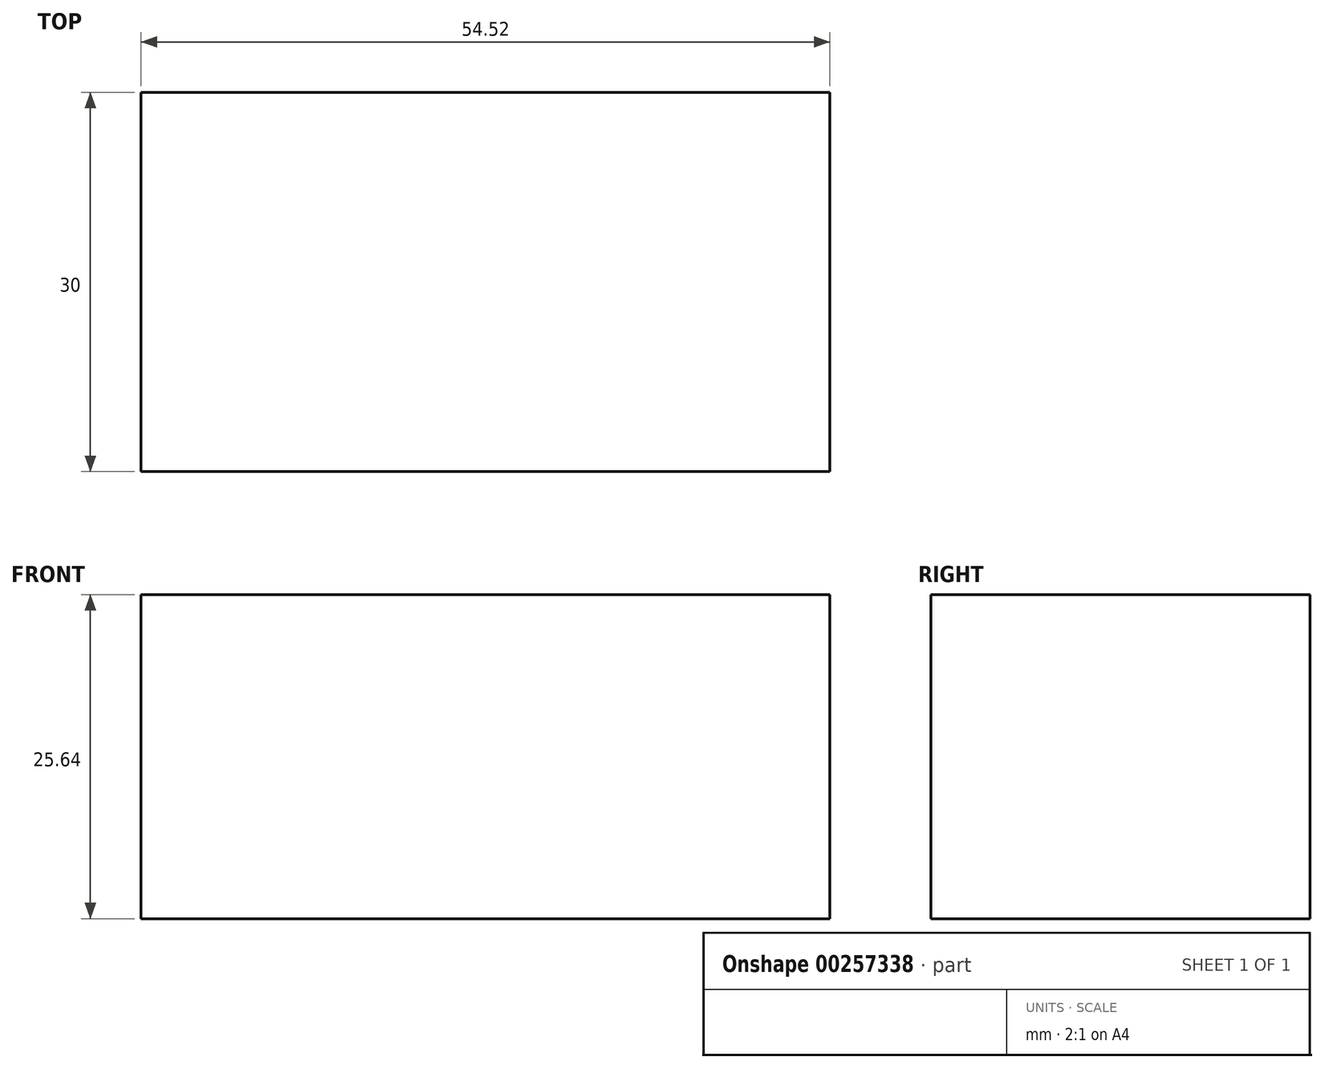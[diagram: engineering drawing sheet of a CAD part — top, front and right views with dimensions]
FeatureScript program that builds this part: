
annotation { "Feature Type Name" : "Feature", "Feature Type Description" : "" }
export const myFeature = defineFeature(function(context is Context, id is Id, definition is map)
    precondition{}
    {
        {
            var Q0;
            Q0=qCreatedBy(makeId("Front.planeOp"),FACE);
            var sketch = newSketch(context, id + "F0", { "sketchPlane" : qUnion([Q0])});
            skLineSegment(sketch, "E0.bottom", {"start": v(0, 0) * mm, "end": v(27.26, 0) * mm});
            skLineSegment(sketch, "E0.top", {"start": v(0, 25.64) * mm, "end": v(27.26, 25.64) * mm});
            skLineSegment(sketch, "E0.left", {"start": v(0, 0) * mm, "end": v(0, 25.64) * mm});
            skLineSegment(sketch, "E0.right", {"start": v(27.26, 0) * mm, "end": v(27.26, 25.64) * mm});
            skSolve(sketch);
        }
        {
            var Q0;
            Q0=makeQuery(id+"F0.imprint","IMPRINT",FACE,{"disambiguationData":[TD([[makeQuery(id+"F0.imprint","IMPRINT",EDGE,{"derivedFrom":sQuery(id+"F0.wireOp",EDGE,"E0.bottom")}),1.0]])]});
            extrude(context, id + "F1", {"entities" : qUnion([Q0]), "depth" : 30 * mm});
        }
        {
            var Q0;
            Q0=makeQuery(id+"F1.opExtrude","SWEPT_BODY",BODY,{"disambiguationData":[OSD([sQuery(id+"F0.wireOp",EDGE,"E0.bottom"),sQuery(id+"F0.wireOp",EDGE,"E0.top"),sQuery(id+"F0.wireOp",EDGE,"E0.left"),sQuery(id+"F0.wireOp",EDGE,"E0.right")])]});
            var Q1;
            Q1=qCreatedBy(makeId("Right.planeOp"),FACE);
            mirror(context, id + "F2", {"operationType" : NewBodyOperationType.ADD, "entities" : qUnion([Q0]), "mirrorPlane" : qUnion([Q1])});
        }
    });
